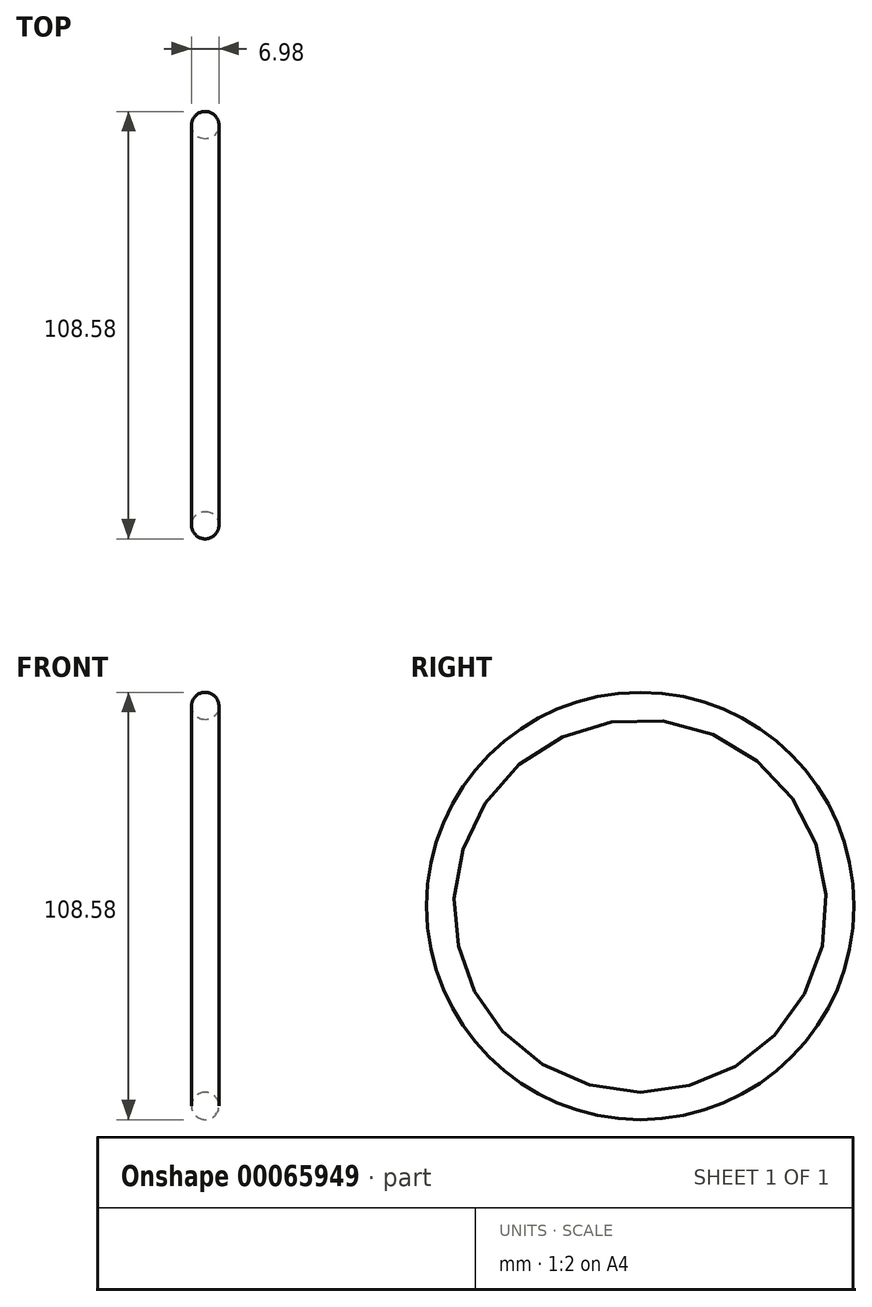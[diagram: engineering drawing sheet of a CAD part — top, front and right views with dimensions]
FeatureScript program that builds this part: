
annotation { "Feature Type Name" : "Feature", "Feature Type Description" : "" }
export const myFeature = defineFeature(function(context is Context, id is Id, definition is map)
    precondition{}
    {
        {
            var Q0;
            Q0=qCreatedBy(makeId("Front.planeOp"),FACE);
            var sketch = newSketch(context, id + "F0", { "sketchPlane" : qUnion([Q0])});
            skLineSegment(sketch, "E0", {"start": v(0, 0) * mm, "end": v(-6.06, 0) * mm, "construction": true});
            skCircle(sketch, "E1", {"center": v(0, 50.8) * mm, "radius": 3.5 * mm});
            skSolve(sketch);
        }
        {
            var Q0;
            Q0=makeQuery(id+"F0.imprint","IMPRINT",FACE,{"disambiguationData":[TD([[makeQuery(id+"F0.imprint","IMPRINT",EDGE,{"derivedFrom":sQuery(id+"F0.wireOp",EDGE,"E1")}),1.0]])]});
            var Q1;
            Q1=sQuery(id+"F0.wireOp",EDGE,"E0");
            revolve(context, id + "F1", {"entities" : qUnion([Q0]), "axis" : qUnion([Q1]), "revolveType" : RevolveType.FULL});
        }
    });
